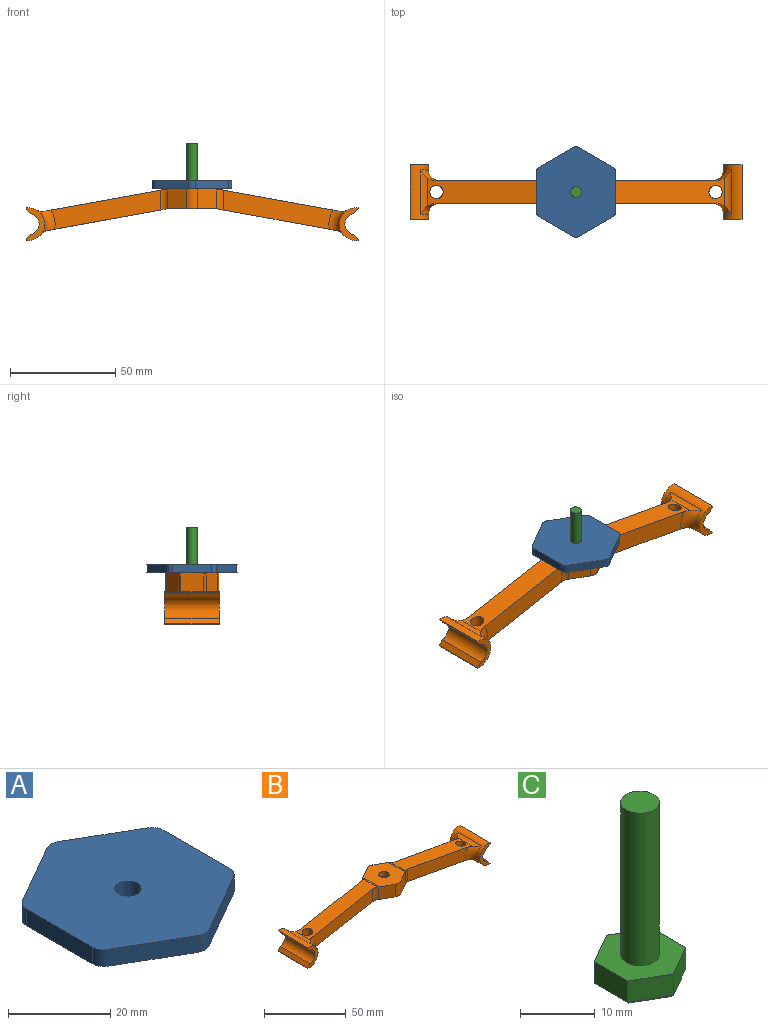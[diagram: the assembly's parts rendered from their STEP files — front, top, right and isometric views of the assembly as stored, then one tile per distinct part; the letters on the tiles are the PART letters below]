
ASSEMBLY  parts=3 mates=4
PART A: 15 faces, bbox 37.9x42.8x4 mm
  f0: plane 15.94x9.2mm, normal (0.5,-0.87,0), area 74mm2, adj f7,f8,f9,f14
  f1: plane 18.41x4.02mm, normal (1,0,0), area 74mm2, adj f7,f8,f9,f10
  f2: plane 15.94x9.2mm, normal (0.5,0.87,0), area 74mm2, adj f7,f8,f10,f11
  f3: plane 15.94x9.2mm, normal (-0.5,0.87,0), area 74mm2, adj f7,f8,f11,f12
  f4: plane 18.41x4.02mm, normal (-1,0,0), area 74mm2, adj f7,f8,f12,f13
  f5: cylinder r=2.58mm len=5.17mm, axis (0,0,-1), area 65.3mm2, adj f7,f8
  f6: plane 15.94x9.2mm, normal (-0.5,-0.87,0), area 74mm2, adj f7,f8,f13,f14
  f7: plane 42.81x37.88mm, normal (0,0,1), area 1218.8mm2, adj f0,f1,f2,f3,f4,f5,f6,f9
  f8: plane 42.81x37.88mm, normal (0,0,-1), area 1218.8mm2, adj f0,f1,f2,f3,f4,f5,f6,f9
  f9: cylinder r=3mm len=4.02mm, axis (0,0,-1), area 12.6mm2, adj f0,f1,f7,f8
  f10: cylinder r=3mm len=4.02mm, axis (0,0,-1), area 12.6mm2, adj f1,f2,f7,f8
  f11: cylinder r=3mm len=4.02mm, axis (0,0,-1), area 12.6mm2, adj f2,f3,f7,f8
  f12: cylinder r=3mm len=4.02mm, axis (0,0,-1), area 12.6mm2, adj f3,f4,f7,f8
  f13: cylinder r=3mm len=4.02mm, axis (0,0,-1), area 12.6mm2, adj f4,f6,f7,f8
  f14: cylinder r=3mm len=4.02mm, axis (0,0,-1), area 12.6mm2, adj f0,f6,f7,f8
PART B: 70 faces, bbox 157.6x28.2x27.9 mm
  f0: cylinder r=3.14mm len=6.27mm, axis (0,0,-1), area 67mm2, adj f6,f63
  f1: cylinder r=5mm len=20.92mm, axis (0,1,0), area 58.2mm2, adj f20,f29,f36,f37,f48
  f2: plane 9.42x9.17mm, normal (0.5,-0.87,0), area 99.5mm2, adj f6,f7,f39,f40,f41,f47
  f3: plane 9.42x9.17mm, normal (0.5,0.87,0), area 99.5mm2, adj f6,f7,f40,f41,f42,f46
  f4: plane 9.4x9.17mm, normal (-0.5,0.87,0), area 99.5mm2, adj f6,f7,f43,f45,f46
  f5: plane 9.4x9.17mm, normal (-0.5,-0.87,0), area 99.5mm2, adj f6,f7,f44,f45,f47
  f6: plane 25.4x22.44mm, normal (0,0,1), area 425.8mm2, adj f0,f2,f3,f4,f5,f40,f45,f46
  f7: plane 25.4x22.89mm, normal (0,0,-1), area 237.9mm2, adj f2,f3,f4,f5,f17,f41,f46,f47
  f8: cylinder r=7.81mm len=25.8mm, axis (0,1,0), area 407mm2, adj f9,f10,f12,f13,f32,f33,f34,f35
  f9: plane 15.62x8.81mm, normal (0,-1,0), area 54.4mm2, adj f8,f11,f12,f13,f14,f15
  f10: plane 15.62x8.81mm, normal (0,1,0), area 54.4mm2, adj f8,f11,f12,f13,f14,f15
  f11: cylinder r=5.18mm len=25.8mm, axis (0,-1,0), area 368.3mm2, adj f9,f10,f14,f15
  f12: plane 25.8x0.24mm, normal (-1,0,0), area 6.2mm2, adj f8,f9,f10,f14
  f13: plane 25.8x0.24mm, normal (-1,0,0), area 6.2mm2, adj f8,f9,f10,f15
  f14: plane 25.8x2.42mm, normal (-0.77,0,0.64), area 80.9mm2, adj f9,f10,f11,f12
  f15: plane 25.8x2.42mm, normal (-0.77,0,-0.64), area 80.9mm2, adj f9,f10,f11,f13
  f16: plane 58.28x13.33mm, normal (-0.18,0,0.98), area 618.4mm2, adj f18,f19,f33,f34,f35,f43,f44,f45
  f17: plane 57.06x13.61mm, normal (0.18,0,-0.98), area 607.9mm2, adj f7,f18,f19,f32,f33,f34,f43,f44
  f18: plane 51.81x18.52mm, normal (0,1,0), area 473.8mm2, adj f16,f17,f33,f43
  f19: plane 51.81x18.52mm, normal (0,-1,0), area 473.8mm2, adj f16,f17,f34,f44
  f20: cylinder r=7.81mm len=25.8mm, axis (0,1,0), area 407mm2, adj f1,f21,f22,f24,f25,f36,f37,f38
  f21: plane 15.62x8.81mm, normal (0,-1,0), area 54.4mm2, adj f20,f23,f24,f25,f26,f27
  f22: plane 15.62x8.81mm, normal (0,1,0), area 54.4mm2, adj f20,f23,f24,f25,f26,f27
  f23: cylinder r=5.18mm len=25.8mm, axis (0,-1,0), area 368.3mm2, adj f21,f22,f26,f27
  f24: plane 25.8x0.24mm, normal (1,0,0), area 6.2mm2, adj f20,f21,f22,f26
  f25: plane 25.8x0.24mm, normal (1,0,0), area 6.2mm2, adj f20,f21,f22,f27
  f26: plane 25.8x2.42mm, normal (0.77,0,0.64), area 80.9mm2, adj f21,f22,f23,f24
  f27: plane 25.8x2.42mm, normal (0.77,0,-0.64), area 80.9mm2, adj f21,f22,f23,f25
  f28: plane 58.28x13.33mm, normal (0.18,0,0.98), area 618.4mm2, adj f30,f31,f36,f37,f38,f39,f40,f42
  f29: plane 56.62x13.33mm, normal (-0.18,0,-0.98), area 602mm2, adj f1,f30,f31,f36,f37,f39,f41,f42
  f30: plane 51.81x18.52mm, normal (0,1,0), area 473.8mm2, adj f28,f29,f37,f42
  f31: plane 51.81x18.52mm, normal (0,-1,0), area 473.8mm2, adj f28,f29,f36,f39
  f32: cylinder r=5mm len=20.92mm, axis (0,1,0), area 58.2mm2, adj f8,f17,f33,f34,f49
  f33: torus R=12.81mm, axis (0,-1,0), area 81.3mm2, adj f8,f16,f17,f18,f32,f35
  f34: torus R=12.81mm, axis (0,-1,0), area 81.3mm2, adj f8,f16,f17,f19,f32,f35
  f35: cylinder r=5mm len=20.92mm, axis (0,1,0), area 60.2mm2, adj f8,f16,f33,f34
  f36: torus R=12.81mm, axis (0,-1,0), area 81.3mm2, adj f1,f20,f28,f29,f31,f38
  f37: torus R=12.81mm, axis (0,-1,0), area 81.3mm2, adj f1,f20,f28,f29,f30,f38
  f38: cylinder r=5mm len=20.92mm, axis (0,1,0), area 60.2mm2, adj f20,f28,f36,f37
  f39: cylinder r=5mm len=9.99mm, axis (0,0,-1), area 34.4mm2, adj f2,f28,f29,f31,f40,f41
  f40: cylinder r=5mm len=14mm, axis (0,1,0), area 12.1mm2, adj f2,f3,f6,f28,f39,f42
  f41: cylinder r=5mm len=14mm, axis (0,1,0), area 12.1mm2, adj f2,f3,f7,f29,f39,f42
  f42: cylinder r=5mm len=9.99mm, axis (0,0,1), area 34.4mm2, adj f3,f28,f29,f30,f40,f41
  f43: cylinder r=5mm len=9.99mm, axis (0,0,-1), area 34.4mm2, adj f4,f16,f17,f18,f45
  f44: cylinder r=5mm len=9.99mm, axis (0,0,1), area 34.4mm2, adj f5,f16,f17,f19,f45
  f45: cylinder r=5mm len=14mm, axis (0,1,0), area 12.1mm2, adj f4,f5,f6,f16,f43,f44
  f46: cylinder r=5mm len=9.4mm, axis (0,0,-1), area 49.2mm2, adj f3,f4,f6,f7
  f47: cylinder r=5mm len=9.4mm, axis (0,0,-1), area 49.2mm2, adj f2,f5,f6,f7
  f48: cylinder r=3.12mm len=10.59mm, axis (0,0,1), area 184.7mm2, adj f1,f28,f29
  f49: cylinder r=3.12mm len=10.59mm, axis (0,0,1), area 184.7mm2, adj f16,f17,f32
  f50: plane 5.11x3mm, normal (-0.5,-0.87,0), area 17.7mm2, adj f7,f56,f64,f69
  f51: plane 5.9x3mm, normal (-1,0,0), area 17.7mm2, adj f7,f56,f64,f65
  f52: plane 5.11x3mm, normal (-0.5,0.87,0), area 17.7mm2, adj f7,f56,f65,f66
  f53: plane 5.11x3mm, normal (0.5,0.87,0), area 17.7mm2, adj f7,f56,f66,f67
  f54: plane 5.9x3mm, normal (1,0,0), area 17.7mm2, adj f7,f56,f67,f68
  f55: plane 5.11x3mm, normal (0.5,-0.87,0), area 17.7mm2, adj f7,f56,f68,f69
  f56: plane 17.8x16.22mm, normal (0,0,-1), area 120.2mm2, adj f50,f51,f52,f53,f54,f55,f57,f58
  f57: plane 5.5x3.18mm, normal (-0.5,-0.87,0), area 19mm2, adj f56,f58,f62,f63
  f58: plane 6.35x3mm, normal (-1,0,0), area 19mm2, adj f56,f57,f59,f63
  f59: plane 5.5x3.18mm, normal (-0.5,0.87,0), area 19mm2, adj f56,f58,f60,f63
  f60: plane 5.5x3.18mm, normal (0.5,0.87,0), area 19mm2, adj f56,f59,f61,f63
  f61: plane 6.35x3mm, normal (1,0,0), area 19mm2, adj f56,f60,f62,f63
  f62: plane 5.5x3.18mm, normal (0.5,-0.87,0), area 19mm2, adj f56,f57,f61,f63
  f63: plane 12.7x11mm, normal (0,0,-1), area 73.9mm2, adj f0,f57,f58,f59,f60,f61,f62
  f64: cylinder r=3mm len=3mm, axis (0,0,1), area 9.4mm2, adj f7,f50,f51,f56
  f65: cylinder r=3mm len=3mm, axis (0,0,1), area 9.4mm2, adj f7,f51,f52,f56
  f66: cylinder r=3mm len=3mm, axis (0,0,1), area 9.4mm2, adj f7,f52,f53,f56
  f67: cylinder r=3mm len=3mm, axis (0,0,1), area 9.4mm2, adj f7,f53,f54,f56
  f68: cylinder r=3mm len=3mm, axis (0,0,1), area 9.4mm2, adj f7,f54,f55,f56
  f69: cylinder r=3mm len=3mm, axis (0,0,1), area 9.4mm2, adj f7,f50,f55,f56
PART C: 16 faces, bbox 11x12.7x29 mm
  f0: plane 5.49x3.5mm, normal (0.5,-0.87,0), area 22.2mm2, adj f1,f5,f6,f13
  f1: plane 6.34x3.5mm, normal (1,0,0), area 22.2mm2, adj f0,f2,f6,f12
  f2: plane 5.49x3.5mm, normal (0.5,0.87,0), area 22.2mm2, adj f1,f3,f6,f10
  f3: plane 5.49x3.5mm, normal (-0.5,0.87,0), area 22.2mm2, adj f2,f4,f6,f8
  f4: plane 6.34x3.5mm, normal (-1,0,0), area 22.2mm2, adj f3,f5,f6,f9
  f5: plane 5.49x3.5mm, normal (-0.5,-0.87,0), area 22.2mm2, adj f0,f4,f6,f11
  f6: plane 12.68x10.98mm, normal (0,0,1), area 83.4mm2, adj f0,f1,f2,f3,f4,f5,f14
  f7: plane 11.53x9.98mm, normal (0,0,-1), area 86.3mm2, adj f8,f9,f10,f11,f12,f13
  f8: plane 5.49x3.46mm, normal (-0.35,0.61,-0.71), area 4.3mm2, adj f3,f7,f9,f10
  f9: plane 6.34x0.5mm, normal (-0.71,0,-0.71), area 4.3mm2, adj f4,f7,f8,f11
  f10: plane 5.49x3.46mm, normal (0.35,0.61,-0.71), area 4.3mm2, adj f2,f7,f8,f12
  f11: plane 5.49x3.46mm, normal (-0.35,-0.61,-0.71), area 4.3mm2, adj f5,f7,f9,f13
  f12: plane 6.34x0.5mm, normal (0.71,0,-0.71), area 4.3mm2, adj f1,f7,f10,f13
  f13: plane 5.49x3.46mm, normal (0.35,-0.61,-0.71), area 4.3mm2, adj f0,f7,f11,f12
  f14: cylinder r=2.58mm len=25mm, axis (0,0,-1), area 406.1mm2, adj f6,f15
  f15: plane 5.17x5.17mm, normal (0,0,1), area 21mm2, adj f14
PLACE A t=(-7.93,-26.69,15.39)mm
PLACE B t=(-7.93,-26.69,5.99)mm
PLACE C t=(-7.93,-26.69,7.99)mm
MATE slider B.f0 <-> C.f14  axis (0,0,1) through (-7.93,-26.69,15.39)mm
MATE fastened A.f5 <-> B.f0  axis (0,0,-1) through (-7.93,-26.69,15.39)mm
MATE slider A.f5 <-> C.f14  axis (0,0,-1) through (-7.93,-26.69,15.39)mm
MATE fastened C.f14 <-> B.f0  axis (0,0,-1) through (-7.93,-26.69,11.99)mm
